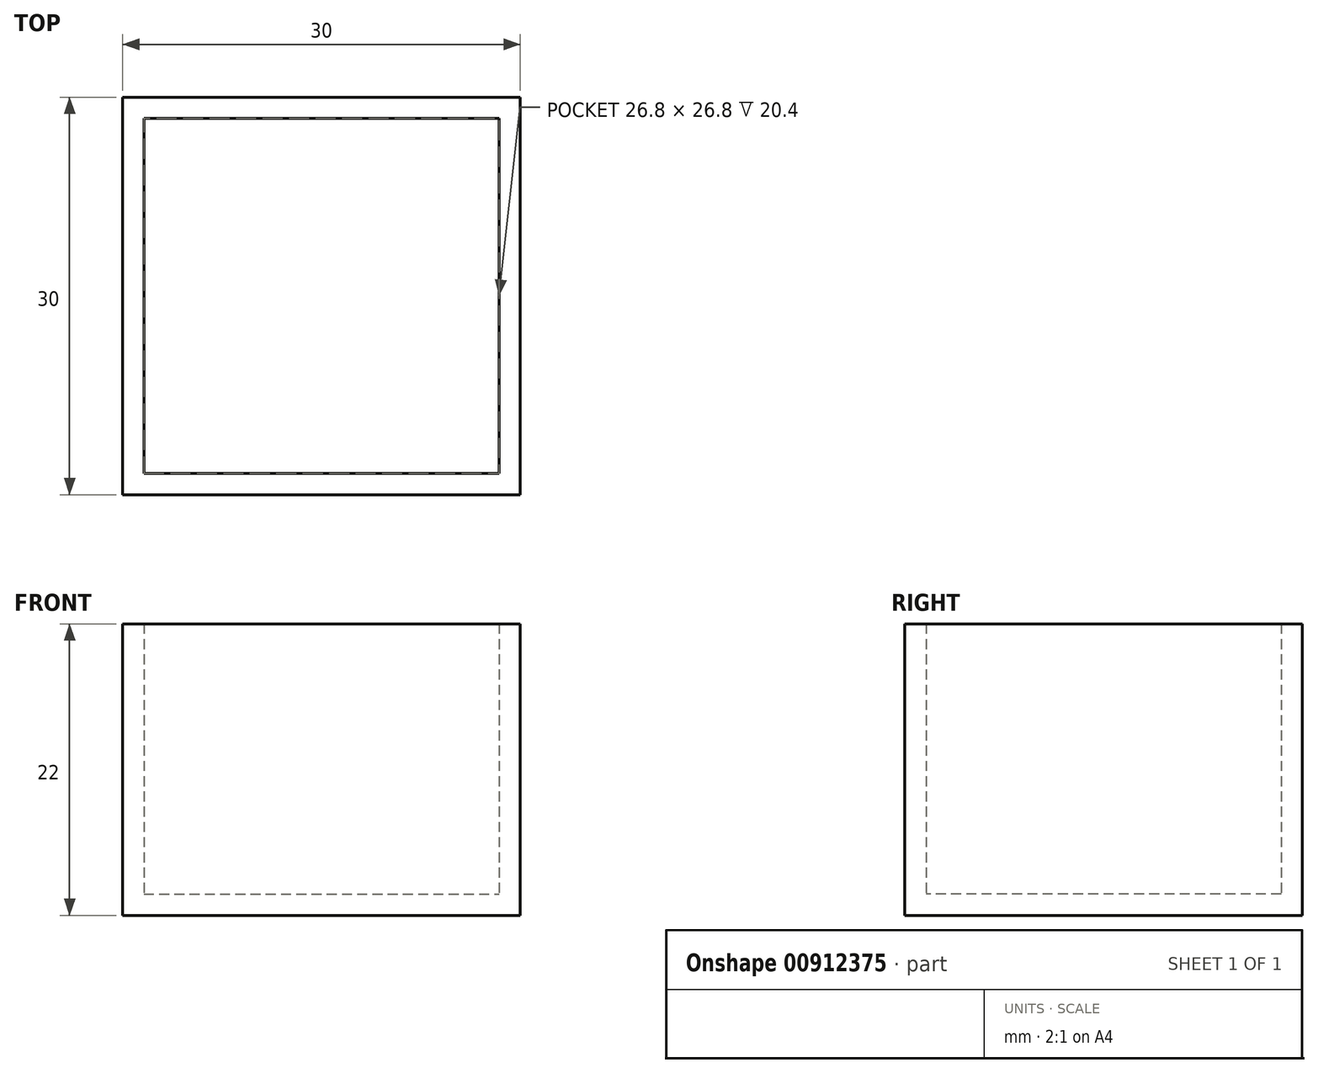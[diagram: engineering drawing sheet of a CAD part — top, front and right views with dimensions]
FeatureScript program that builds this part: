
annotation { "Feature Type Name" : "Feature", "Feature Type Description" : "" }
export const myFeature = defineFeature(function(context is Context, id is Id, definition is map)
    precondition{}
    {
        {
            var Q0;
            Q0=qCreatedBy(makeId("Top.planeOp"),FACE);
            var sketch = newSketch(context, id + "F0", { "sketchPlane" : qUnion([Q0])});
            skLineSegment(sketch, "E0.bottom", {"start": v(-15, 15) * mm, "end": v(15, 15) * mm});
            skLineSegment(sketch, "E0.top", {"start": v(-15, -15) * mm, "end": v(15, -15) * mm});
            skLineSegment(sketch, "E0.left", {"start": v(-15, 15) * mm, "end": v(-15, -15) * mm});
            skLineSegment(sketch, "E0.right", {"start": v(15, 15) * mm, "end": v(15, -15) * mm});
            skPoint(sketch, "E1", {"position": v(0, 15) * mm});
            skPoint(sketch, "E2", {"position": v(-15, 0) * mm});
            skSolve(sketch);
        }
        {
            var Q0;
            Q0=makeQuery(id+"F0.imprint","IMPRINT",FACE,{"disambiguationData":[TD([[makeQuery(id+"F0.imprint","IMPRINT",EDGE,{"derivedFrom":sQuery(id+"F0.wireOp",EDGE,"E0.bottom")}),-1.0]])]});
            extrude(context, id + "F1", {"entities" : qUnion([Q0]), "depth" : 22 * mm, "offsetDistance" : 25 * mm});
        }
        {
            var Q0;
            Q0=makeQuery(id+"F1.opExtrude","CAP_FACE",FACE,{"disambiguationData":[OSD([sQuery(id+"F0.wireOp",EDGE,"E0.bottom"),sQuery(id+"F0.wireOp",EDGE,"E0.top"),sQuery(id+"F0.wireOp",EDGE,"E0.left"),sQuery(id+"F0.wireOp",EDGE,"E0.right")])],"isStart":false});
            shell(context, id + "F2", {"entities" : qUnion([Q0]), "thickness" : 1.6 * mm});
        }
    });
